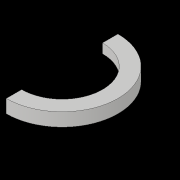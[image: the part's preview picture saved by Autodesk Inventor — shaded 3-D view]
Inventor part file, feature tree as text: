
AUTODESK INVENTOR PART (.ipt)
format: ipt  version: 2017 (Build 210142000, 142)  size: 114,176 bytes
history: native  units: in
note: dims shown in document units (in); Inventor stores cm internally (conversion verified against a paired STEP export)
features: revolve x1, sketch x1
ambient origin geometry x8: Origin, YZ Plane, XZ Plane, XY Plane, X Axis, Y Axis, Z Axis, Center Point
bodies: Solid1 (feature_tree)
feature tree (2):
  revolve  "Revolution1"  [1 undecoded]
  sketch  "Sketch1"  dims[d0=2.0in d2=10.5in d3=2.0in d4=2.875in d5=0.125in d6=0.125in d7=0.125in d8=0.125in d9=0.125in d10=0.125in d11=0.125in d12=0.125in d13=1.0285in d14=0.5in d15=180.0deg d16=5.25in d17=0.125in d18=0.125in d19=0.25in d20=0.0625in d21=0.25in d22=0.25in]
note: 1 required parameter value undecoded (feature->parameter linkage not recoverable at this tier; creation-order binding heuristic only, values carry confidence <= 0.55)
